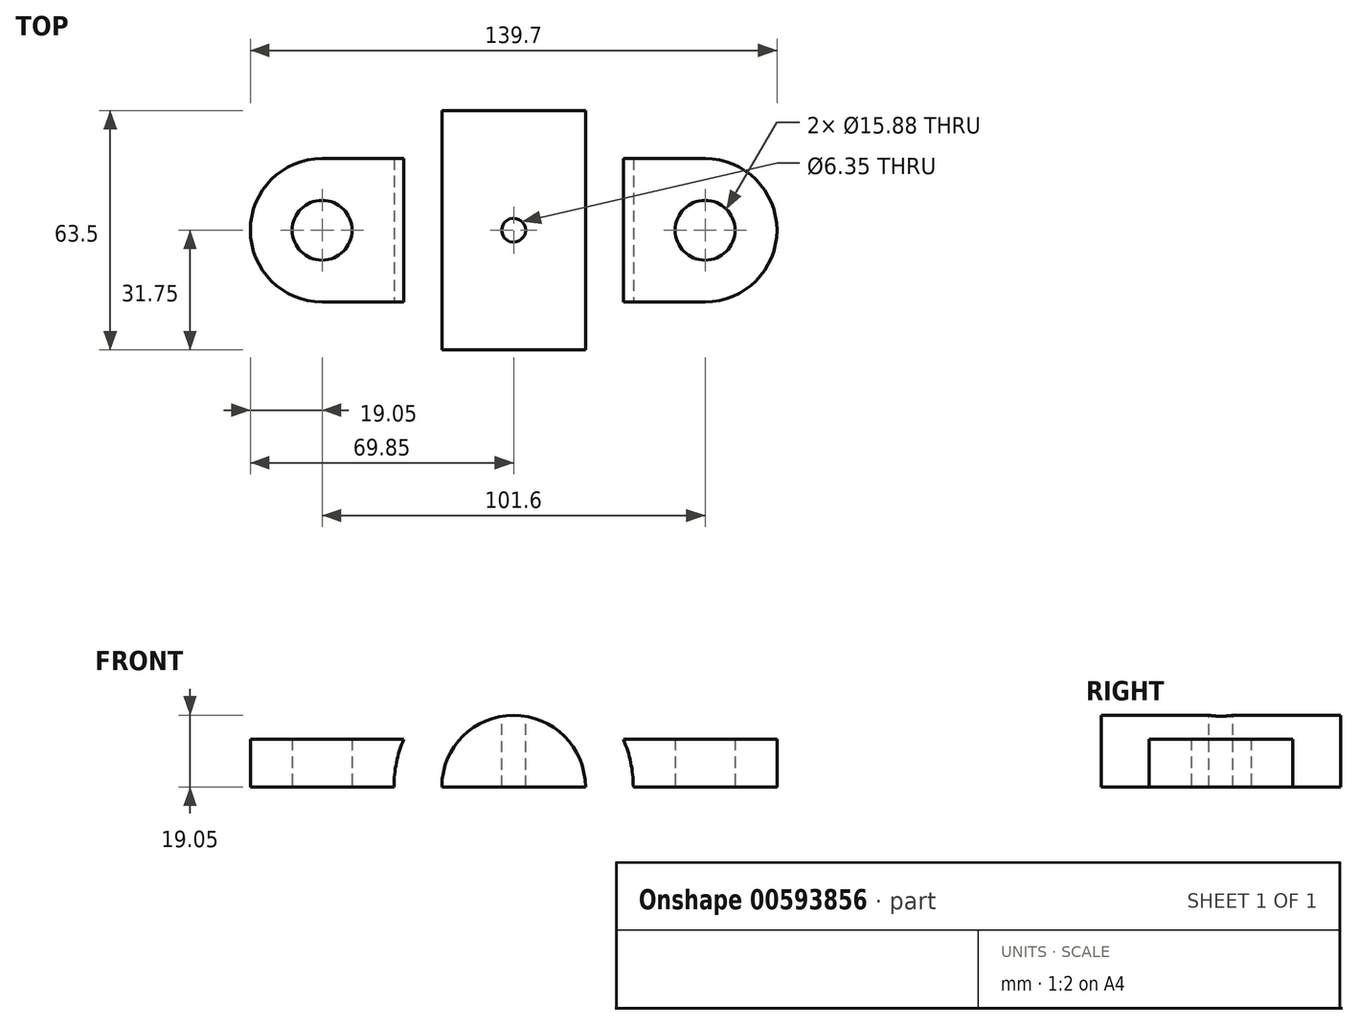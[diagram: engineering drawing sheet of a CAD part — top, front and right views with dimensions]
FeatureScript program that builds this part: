
annotation { "Feature Type Name" : "Feature", "Feature Type Description" : "" }
export const myFeature = defineFeature(function(context is Context, id is Id, definition is map)
    precondition{}
    {
        {
            var Q0;
            Q0=qCreatedBy(makeId("Front.planeOp"),FACE);
            var sketch = newSketch(context, id + "F0", { "sketchPlane" : qUnion([Q0])});
            skArc(sketch, "E0", {"start": v(-19.05, 0) * mm, "mid": v(0, 19.05) * mm, "end": v(19.05, 0) * mm});
            skArc(sketch, "E1", {"start": v(-31.75, 0) * mm, "mid": v(0, 31.75) * mm, "end": v(31.75, 0) * mm});
            skLineSegment(sketch, "E2", {"start": v(-31.75, 0) * mm, "end": v(-19.05, 0) * mm});
            skLineSegment(sketch, "E3", {"start": v(19.05, 0) * mm, "end": v(31.75, 0) * mm});
            skLineSegment(sketch, "E4", {"start": v(-19.05, 0) * mm, "end": v(19.05, 0) * mm});
            skSolve(sketch);
        }
        {
            var Q0;
            Q0=makeQuery(id+"F0.imprint","IMPRINT",FACE,{"disambiguationData":[TD([[makeQuery(id+"F0.imprint","IMPRINT",EDGE,{"derivedFrom":sQuery(id+"F0.wireOp",EDGE,"E0")}),1.0]])]});
            extrude(context, id + "F1", {"entities" : qUnion([Q0]), "endBound" : BoundingType.SYMMETRIC, "depth" : 63.5 * mm, "offsetDistance" : 25.4 * mm});
        }
        {
            var Q0;
            Q0=qCreatedBy(makeId("Top.planeOp"),FACE);
            var sketch = newSketch(context, id + "F2", { "sketchPlane" : qUnion([Q0])});
            skLineSegment(sketch, "E5", {"start": v(0, 0) * mm, "end": v(50.8, 0) * mm, "construction": true});
            skLineSegment(sketch, "E6", {"start": v(0, 0) * mm, "end": v(-50.8, 0) * mm, "construction": true});
            skArc(sketch, "E7", {"start": v(-50.8, 19.05) * mm, "mid": v(-69.85, 0) * mm, "end": v(-50.8, -19.05) * mm});
            skArc(sketch, "E8", {"start": v(50.8, 19.05) * mm, "mid": v(69.85, 0) * mm, "end": v(50.8, -19.05) * mm});
            skLineSegment(sketch, "E9", {"start": v(-50.8, 19.05) * mm, "end": v(50.8, 19.05) * mm});
            skLineSegment(sketch, "E10", {"start": v(-50.8, -19.05) * mm, "end": v(50.8, -19.05) * mm});
            skCircle(sketch, "E11", {"center": v(50.8, 0) * mm, "radius": 7.94 * mm});
            skCircle(sketch, "E12", {"center": v(-50.8, 0) * mm, "radius": 7.94 * mm});
            skSolve(sketch);
        }
        {
            var Q0;
            Q0 = qSketchRegion(id + "F2", true);
            extrude(context, id + "F3", {"entities" : qUnion([Q0]), "operationType" : NewBodyOperationType.ADD, "depth" : 12.7 * mm, "offsetDistance" : 25.4 * mm});
        }
        {
            var Q0;
            Q0=makeQuery(id+"F0.imprint","IMPRINT",FACE,{"disambiguationData":[TD([[makeQuery(id+"F0.imprint","IMPRINT",EDGE,{"derivedFrom":sQuery(id+"F0.wireOp",EDGE,"E0")}),-1.0]])]});
            var Q1;
            {var subQ3=sQuery(id+"F2.wireOp",EDGE,"E9");Q1=makeQuery(id+"F3.boolean.opBoolean","SPLIT",FACE,{"disambiguationData":[TD([makeQuery(id+"F1.opExtrude","SWEPT_FACE",FACE,{"disambiguationData":[OSD([sQuery(id+"F0.wireOp",EDGE,"E0")])]})])],"derivedFrom":makeQuery(id+"F3.opExtrude","SWEPT_FACE",FACE,{"disambiguationData":[OSD([subQ3])]})});}
            var Q2;
            {var subQ2=sQuery(id+"F2.wireOp",EDGE,"E10");Q2=makeQuery(id+"F3.boolean.opBoolean","SPLIT",FACE,{"disambiguationData":[TD([makeQuery(id+"F1.opExtrude","SWEPT_FACE",FACE,{"disambiguationData":[OSD([sQuery(id+"F0.wireOp",EDGE,"E0")])]})])],"derivedFrom":makeQuery(id+"F3.opExtrude","SWEPT_FACE",FACE,{"disambiguationData":[OSD([subQ2])]})});}
            extrude(context, id + "F4", {"entities" : qUnion([Q0]), "operationType" : NewBodyOperationType.REMOVE, "endBound" : BoundingType.UP_TO_SURFACE, "oppositeDirection" : true, "depth" : 25.4 * mm, "endBoundEntityFace" : qUnion([Q1]), "offsetDistance" : 25.4 * mm, "hasSecondDirection" : true, "secondDirectionBound" : SecondDirectionBoundingType.UP_TO_SURFACE, "secondDirectionOppositeDirection" : false, "secondDirectionDepth" : 25.4 * mm, "secondDirectionBoundEntityFace" : qUnion([Q2])});
        }
        {
            var Q0;
            Q0=qCreatedBy(makeId("Top.planeOp"),FACE);
            cPlane(context, id + "F5", {"entities" : qUnion([Q0]), "cplaneType" : CPlaneType.OFFSET, "offset" : 31.75 * mm, "width" : 152.4 * mm, "height" : 152.4 * mm});
        }
        {
            var Q0;
            Q0=qCreatedBy(id+"F5.planeOp",FACE);
            var sketch = newSketch(context, id + "F6", { "sketchPlane" : qUnion([Q0])});
            skPoint(sketch, "E13", {"position": v(0, 0) * mm});
            skSolve(sketch);
        }
        {
            var Q0;
            Q0=sQuery(id+"F6.wireOp",VERTEX,"E13");
            var Q1;
            Q1=makeQuery(id+"F1.opExtrude","SWEPT_BODY",BODY,{"disambiguationData":[OSD([sQuery(id+"F0.wireOp",EDGE,"E0"),sQuery(id+"F0.wireOp",EDGE,"E1"),sQuery(id+"F0.wireOp",EDGE,"E2"),sQuery(id+"F0.wireOp",EDGE,"E3")])]});
            hole(context, id + "F7", {"style" : HoleStyle.SIMPLE, "endStyle" : HoleEndStyle.THROUGH, "holeDiameter" : 6.35 * mm, "majorDiameter" : 6.35 * mm, "isTappedThrough" : true, "tappedDepth" : 12.7 * mm, "tapClearance" : 3, "locations" : qUnion([Q0]), "scope" : qUnion([Q1])});
        }
    });
